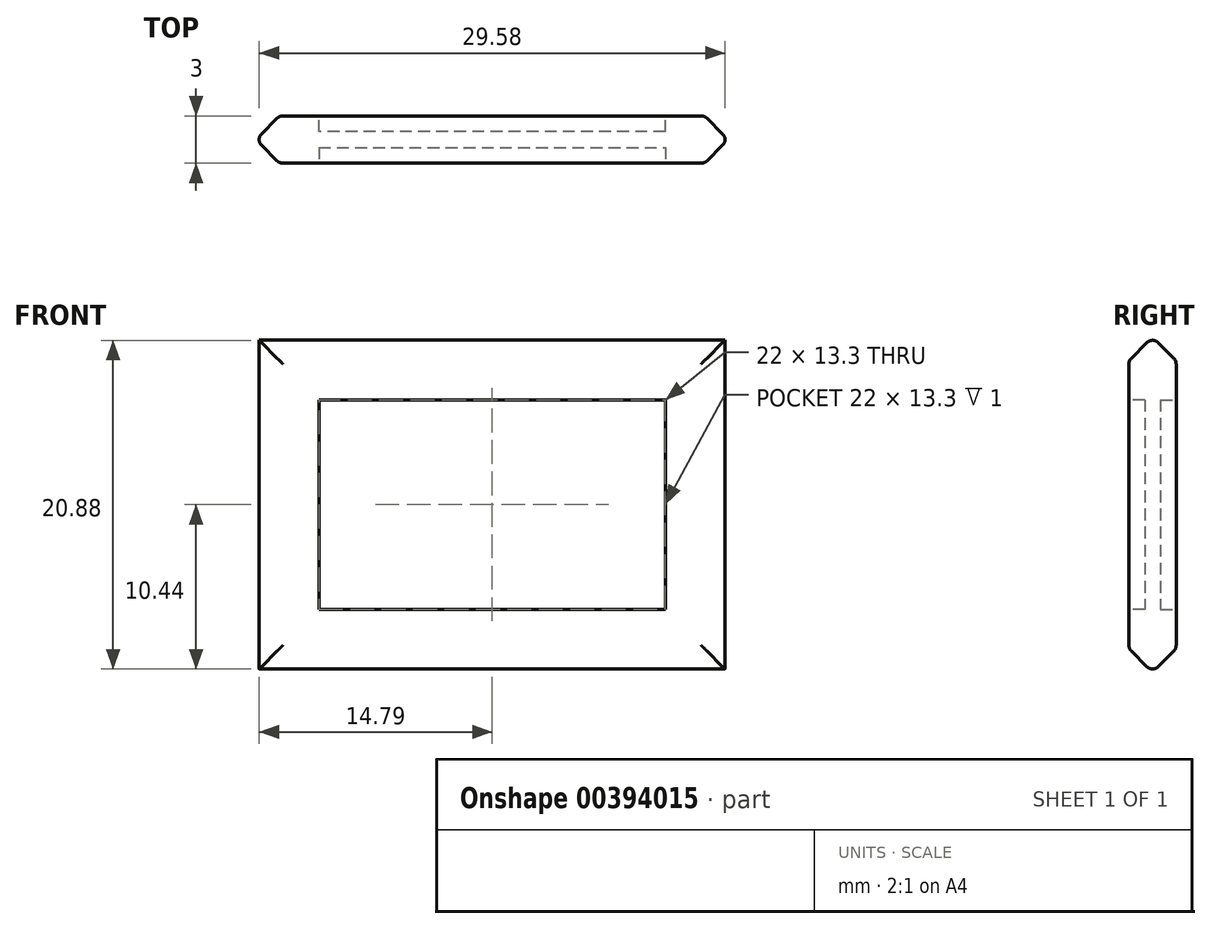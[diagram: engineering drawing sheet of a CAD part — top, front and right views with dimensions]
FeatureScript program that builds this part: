
annotation { "Feature Type Name" : "Feature", "Feature Type Description" : "" }
export const myFeature = defineFeature(function(context is Context, id is Id, definition is map)
    precondition{}
    {
        {
            var Q0;
            Q0=qCreatedBy(makeId("Front.planeOp"),FACE);
            var sketch = newSketch(context, id + "F0", { "sketchPlane" : qUnion([Q0])});
            skLineSegment(sketch, "E0.bottom", {"start": v(-15, 10.65) * mm, "end": v(15, 10.65) * mm});
            skLineSegment(sketch, "E0.top", {"start": v(-15, -10.65) * mm, "end": v(15, -10.65) * mm});
            skLineSegment(sketch, "E0.left", {"start": v(-15, 10.65) * mm, "end": v(-15, -10.65) * mm});
            skLineSegment(sketch, "E0.right", {"start": v(15, 10.65) * mm, "end": v(15, -10.65) * mm});
            skSolve(sketch);
        }
        {
            var Q0;
            Q0=qSketchRegion(id+"F0",true);
            extrude(context, id + "F1", {"entities" : qUnion([Q0]), "depth" : 3 * mm});
        }
        {
            var Q0;
            Q0=makeQuery(id+"F1.opExtrude","CAP_FACE",FACE,{"disambiguationData":[OSD([sQuery(id+"F0.wireOp",EDGE,"E0.bottom"),sQuery(id+"F0.wireOp",EDGE,"E0.top"),sQuery(id+"F0.wireOp",EDGE,"E0.left"),sQuery(id+"F0.wireOp",EDGE,"E0.right")])],"isStart":false});
            var Q1;
            Q1=makeQuery(id+"F1.opExtrude","CAP_FACE",FACE,{"disambiguationData":[OSD([sQuery(id+"F0.wireOp",EDGE,"E0.bottom"),sQuery(id+"F0.wireOp",EDGE,"E0.top"),sQuery(id+"F0.wireOp",EDGE,"E0.left"),sQuery(id+"F0.wireOp",EDGE,"E0.right")])],"isStart":true});
            chamfer(context, id + "F2", {"entities" : qUnion([Q0, Q1]), "width" : 1.5 * mm, "tangentPropagation" : true});
        }
        {
            var Q0;
            Q0=makeQuery(id+"F1.opExtrude","CAP_FACE",FACE,{"disambiguationData":[OSD([sQuery(id+"F0.wireOp",EDGE,"E0.bottom"),sQuery(id+"F0.wireOp",EDGE,"E0.top"),sQuery(id+"F0.wireOp",EDGE,"E0.left"),sQuery(id+"F0.wireOp",EDGE,"E0.right")])],"isStart":true});
            var sketch = newSketch(context, id + "F3", { "sketchPlane" : qUnion([Q0])});
            skLineSegment(sketch, "E1.bottom", {"start": v(-11, 6.65) * mm, "end": v(11, 6.65) * mm});
            skLineSegment(sketch, "E1.top", {"start": v(-11, -6.65) * mm, "end": v(11, -6.65) * mm});
            skLineSegment(sketch, "E1.left", {"start": v(-11, 6.65) * mm, "end": v(-11, -6.65) * mm});
            skLineSegment(sketch, "E1.right", {"start": v(11, 6.65) * mm, "end": v(11, -6.65) * mm});
            skSolve(sketch);
        }
        {
            var Q0;
            Q0=qSketchRegion(id+"F3",true);
            extrude(context, id + "F4", {"entities" : qUnion([Q0]), "operationType" : NewBodyOperationType.REMOVE, "oppositeDirection" : true, "depth" : 1 * mm});
        }
        {
            var Q0;
            Q0=makeQuery(id+"F1.opExtrude","CAP_FACE",FACE,{"disambiguationData":[OSD([sQuery(id+"F0.wireOp",EDGE,"E0.bottom"),sQuery(id+"F0.wireOp",EDGE,"E0.top"),sQuery(id+"F0.wireOp",EDGE,"E0.left"),sQuery(id+"F0.wireOp",EDGE,"E0.right")])],"isStart":false});
            var sketch = newSketch(context, id + "F5", { "sketchPlane" : qUnion([Q0])});
            skLineSegment(sketch, "E2.bottom", {"start": v(-11, 6.65) * mm, "end": v(11, 6.65) * mm});
            skLineSegment(sketch, "E2.top", {"start": v(-11, -6.65) * mm, "end": v(11, -6.65) * mm});
            skLineSegment(sketch, "E2.left", {"start": v(-11, 6.65) * mm, "end": v(-11, -6.65) * mm});
            skLineSegment(sketch, "E2.right", {"start": v(11, 6.65) * mm, "end": v(11, -6.65) * mm});
            skSolve(sketch);
        }
        {
            var Q0;
            Q0=qSketchRegion(id+"F5",true);
            extrude(context, id + "F6", {"entities" : qUnion([Q0]), "operationType" : NewBodyOperationType.REMOVE, "oppositeDirection" : true, "depth" : 1 * mm});
        }
        {
            var Q0;
            {var subQ0=sQuery(id+"F0.wireOp",EDGE,"E0.top");Q0=makeQuery(id+"F2.opChamfer","BLEND_EDGE",EDGE,{"blendedFrom":[makeQuery(id+"F1.opExtrude","CAP_EDGE",EDGE,{"disambiguationData":[OSD([subQ0])],"isStart":true}),makeQuery(id+"F1.opExtrude","CAP_EDGE",EDGE,{"disambiguationData":[OSD([subQ0])],"isStart":false})],"blendedInto":[]});}
            var Q1;
            {var subQ0=sQuery(id+"F0.wireOp",EDGE,"E0.left");Q1=makeQuery(id+"F2.opChamfer","BLEND_EDGE",EDGE,{"blendedFrom":[makeQuery(id+"F1.opExtrude","CAP_EDGE",EDGE,{"disambiguationData":[OSD([subQ0])],"isStart":true}),makeQuery(id+"F1.opExtrude","CAP_EDGE",EDGE,{"disambiguationData":[OSD([subQ0])],"isStart":false})],"blendedInto":[]});}
            var Q2;
            {var subQ0=sQuery(id+"F0.wireOp",EDGE,"E0.bottom");Q2=makeQuery(id+"F2.opChamfer","BLEND_EDGE",EDGE,{"blendedFrom":[makeQuery(id+"F1.opExtrude","CAP_EDGE",EDGE,{"disambiguationData":[OSD([subQ0])],"isStart":true}),makeQuery(id+"F1.opExtrude","CAP_EDGE",EDGE,{"disambiguationData":[OSD([subQ0])],"isStart":false})],"blendedInto":[]});}
            var Q3;
            {var subQ0=sQuery(id+"F0.wireOp",EDGE,"E0.right");Q3=makeQuery(id+"F2.opChamfer","BLEND_EDGE",EDGE,{"blendedFrom":[makeQuery(id+"F1.opExtrude","CAP_EDGE",EDGE,{"disambiguationData":[OSD([subQ0])],"isStart":true}),makeQuery(id+"F1.opExtrude","CAP_EDGE",EDGE,{"disambiguationData":[OSD([subQ0])],"isStart":false})],"blendedInto":[]});}
            fillet(context, id + "F7", {"entities" : qUnion([Q0, Q1, Q2, Q3]), "radius" : 0.5 * mm, "tangentPropagation" : true, "allowEdgeOverflow" : false});
        }
        {
            var Q0;
            {var subQ0=sQuery(id+"F0.wireOp",EDGE,"E0.right");Q0=makeQuery(id+"F2.opChamfer","BLEND_EDGE",EDGE,{"blendedFrom":[makeQuery(id+"F1.opExtrude","CAP_EDGE",EDGE,{"disambiguationData":[OSD([subQ0])],"isStart":true}),makeQuery(id+"F1.opExtrude","CAP_FACE",FACE,{"disambiguationData":[OSD([sQuery(id+"F0.wireOp",EDGE,"E0.bottom"),sQuery(id+"F0.wireOp",EDGE,"E0.top"),sQuery(id+"F0.wireOp",EDGE,"E0.left"),subQ0])],"isStart":true})],"blendedInto":[makeQuery(id+"F1.opExtrude","CAP_FACE",FACE,{"disambiguationData":[OSD([sQuery(id+"F0.wireOp",EDGE,"E0.bottom"),sQuery(id+"F0.wireOp",EDGE,"E0.top"),sQuery(id+"F0.wireOp",EDGE,"E0.left"),subQ0])],"isStart":true})]});}
            var Q1;
            {var subQ0=sQuery(id+"F0.wireOp",EDGE,"E0.bottom");Q1=makeQuery(id+"F2.opChamfer","BLEND_EDGE",EDGE,{"blendedFrom":[makeQuery(id+"F1.opExtrude","CAP_EDGE",EDGE,{"disambiguationData":[OSD([subQ0])],"isStart":true}),makeQuery(id+"F1.opExtrude","CAP_FACE",FACE,{"disambiguationData":[OSD([subQ0,sQuery(id+"F0.wireOp",EDGE,"E0.top"),sQuery(id+"F0.wireOp",EDGE,"E0.left"),sQuery(id+"F0.wireOp",EDGE,"E0.right")])],"isStart":true})],"blendedInto":[makeQuery(id+"F1.opExtrude","CAP_FACE",FACE,{"disambiguationData":[OSD([subQ0,sQuery(id+"F0.wireOp",EDGE,"E0.top"),sQuery(id+"F0.wireOp",EDGE,"E0.left"),sQuery(id+"F0.wireOp",EDGE,"E0.right")])],"isStart":true})]});}
            var Q2;
            {var subQ0=sQuery(id+"F0.wireOp",EDGE,"E0.top");Q2=makeQuery(id+"F2.opChamfer","BLEND_EDGE",EDGE,{"blendedFrom":[makeQuery(id+"F1.opExtrude","CAP_EDGE",EDGE,{"disambiguationData":[OSD([subQ0])],"isStart":true}),makeQuery(id+"F1.opExtrude","CAP_FACE",FACE,{"disambiguationData":[OSD([sQuery(id+"F0.wireOp",EDGE,"E0.bottom"),subQ0,sQuery(id+"F0.wireOp",EDGE,"E0.left"),sQuery(id+"F0.wireOp",EDGE,"E0.right")])],"isStart":true})],"blendedInto":[makeQuery(id+"F1.opExtrude","CAP_FACE",FACE,{"disambiguationData":[OSD([sQuery(id+"F0.wireOp",EDGE,"E0.bottom"),subQ0,sQuery(id+"F0.wireOp",EDGE,"E0.left"),sQuery(id+"F0.wireOp",EDGE,"E0.right")])],"isStart":true})]});}
            var Q3;
            {var subQ0=sQuery(id+"F0.wireOp",EDGE,"E0.left");Q3=makeQuery(id+"F2.opChamfer","BLEND_EDGE",EDGE,{"blendedFrom":[makeQuery(id+"F1.opExtrude","CAP_EDGE",EDGE,{"disambiguationData":[OSD([subQ0])],"isStart":true}),makeQuery(id+"F1.opExtrude","CAP_FACE",FACE,{"disambiguationData":[OSD([sQuery(id+"F0.wireOp",EDGE,"E0.bottom"),sQuery(id+"F0.wireOp",EDGE,"E0.top"),subQ0,sQuery(id+"F0.wireOp",EDGE,"E0.right")])],"isStart":true})],"blendedInto":[makeQuery(id+"F1.opExtrude","CAP_FACE",FACE,{"disambiguationData":[OSD([sQuery(id+"F0.wireOp",EDGE,"E0.bottom"),sQuery(id+"F0.wireOp",EDGE,"E0.top"),subQ0,sQuery(id+"F0.wireOp",EDGE,"E0.right")])],"isStart":true})]});}
            fillet(context, id + "F8", {"entities" : qUnion([Q0, Q1, Q2, Q3]), "radius" : 0.5 * mm, "tangentPropagation" : true, "allowEdgeOverflow" : false});
        }
        {
            var Q0;
            {var subQ0=sQuery(id+"F0.wireOp",EDGE,"E0.left");Q0=makeQuery(id+"F2.opChamfer","BLEND_EDGE",EDGE,{"blendedFrom":[makeQuery(id+"F1.opExtrude","CAP_EDGE",EDGE,{"disambiguationData":[OSD([subQ0])],"isStart":false}),makeQuery(id+"F1.opExtrude","CAP_FACE",FACE,{"disambiguationData":[OSD([sQuery(id+"F0.wireOp",EDGE,"E0.bottom"),sQuery(id+"F0.wireOp",EDGE,"E0.top"),subQ0,sQuery(id+"F0.wireOp",EDGE,"E0.right")])],"isStart":false})],"blendedInto":[makeQuery(id+"F1.opExtrude","CAP_FACE",FACE,{"disambiguationData":[OSD([sQuery(id+"F0.wireOp",EDGE,"E0.bottom"),sQuery(id+"F0.wireOp",EDGE,"E0.top"),subQ0,sQuery(id+"F0.wireOp",EDGE,"E0.right")])],"isStart":false})]});}
            var Q1;
            {var subQ0=sQuery(id+"F0.wireOp",EDGE,"E0.top");Q1=makeQuery(id+"F2.opChamfer","BLEND_EDGE",EDGE,{"blendedFrom":[makeQuery(id+"F1.opExtrude","CAP_EDGE",EDGE,{"disambiguationData":[OSD([subQ0])],"isStart":false}),makeQuery(id+"F1.opExtrude","CAP_FACE",FACE,{"disambiguationData":[OSD([sQuery(id+"F0.wireOp",EDGE,"E0.bottom"),subQ0,sQuery(id+"F0.wireOp",EDGE,"E0.left"),sQuery(id+"F0.wireOp",EDGE,"E0.right")])],"isStart":false})],"blendedInto":[makeQuery(id+"F1.opExtrude","CAP_FACE",FACE,{"disambiguationData":[OSD([sQuery(id+"F0.wireOp",EDGE,"E0.bottom"),subQ0,sQuery(id+"F0.wireOp",EDGE,"E0.left"),sQuery(id+"F0.wireOp",EDGE,"E0.right")])],"isStart":false})]});}
            var Q2;
            {var subQ0=sQuery(id+"F0.wireOp",EDGE,"E0.bottom");Q2=makeQuery(id+"F2.opChamfer","BLEND_EDGE",EDGE,{"blendedFrom":[makeQuery(id+"F1.opExtrude","CAP_EDGE",EDGE,{"disambiguationData":[OSD([subQ0])],"isStart":false}),makeQuery(id+"F1.opExtrude","CAP_FACE",FACE,{"disambiguationData":[OSD([subQ0,sQuery(id+"F0.wireOp",EDGE,"E0.top"),sQuery(id+"F0.wireOp",EDGE,"E0.left"),sQuery(id+"F0.wireOp",EDGE,"E0.right")])],"isStart":false})],"blendedInto":[makeQuery(id+"F1.opExtrude","CAP_FACE",FACE,{"disambiguationData":[OSD([subQ0,sQuery(id+"F0.wireOp",EDGE,"E0.top"),sQuery(id+"F0.wireOp",EDGE,"E0.left"),sQuery(id+"F0.wireOp",EDGE,"E0.right")])],"isStart":false})]});}
            var Q3;
            {var subQ0=sQuery(id+"F0.wireOp",EDGE,"E0.right");Q3=makeQuery(id+"F2.opChamfer","BLEND_EDGE",EDGE,{"blendedFrom":[makeQuery(id+"F1.opExtrude","CAP_EDGE",EDGE,{"disambiguationData":[OSD([subQ0])],"isStart":false}),makeQuery(id+"F1.opExtrude","CAP_FACE",FACE,{"disambiguationData":[OSD([sQuery(id+"F0.wireOp",EDGE,"E0.bottom"),sQuery(id+"F0.wireOp",EDGE,"E0.top"),sQuery(id+"F0.wireOp",EDGE,"E0.left"),subQ0])],"isStart":false})],"blendedInto":[makeQuery(id+"F1.opExtrude","CAP_FACE",FACE,{"disambiguationData":[OSD([sQuery(id+"F0.wireOp",EDGE,"E0.bottom"),sQuery(id+"F0.wireOp",EDGE,"E0.top"),sQuery(id+"F0.wireOp",EDGE,"E0.left"),subQ0])],"isStart":false})]});}
            fillet(context, id + "F9", {"entities" : qUnion([Q0, Q1, Q2, Q3]), "radius" : 0.5 * mm, "tangentPropagation" : true, "allowEdgeOverflow" : false});
        }
    });
